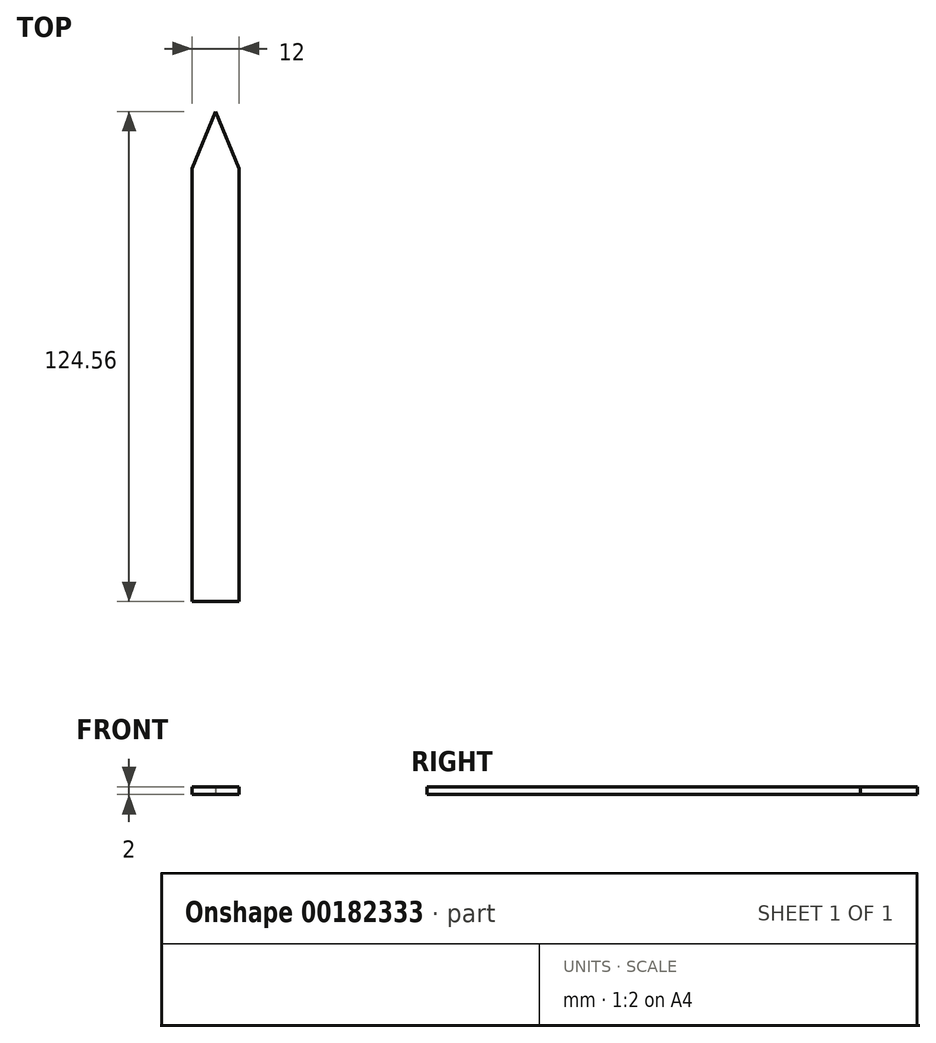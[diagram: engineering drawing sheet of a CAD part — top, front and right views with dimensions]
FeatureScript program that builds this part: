
annotation { "Feature Type Name" : "Feature", "Feature Type Description" : "" }
export const myFeature = defineFeature(function(context is Context, id is Id, definition is map)
    precondition{}
    {
        {
            var Q0;
            Q0=qCreatedBy(makeId("Top.planeOp"),FACE);
            var sketch = newSketch(context, id + "F0", { "sketchPlane" : qUnion([Q0])});
            skLineSegment(sketch, "E0.bottom", {"start": v(-6, -55) * mm, "end": v(0, -55.01) * mm});
            skLineSegment(sketch, "E0.left", {"start": v(-6, -55) * mm, "end": v(-6, 55.02) * mm});
            skLineSegment(sketch, "E0.right", {"start": v(6, -55.02) * mm, "end": v(6, 55) * mm});
            skPoint(sketch, "E0.middle", {"position": v(0, 0) * mm});
            skLineSegment(sketch, "E1.0", {"start": v(0, 69.54) * mm, "end": v(-6, 55.02) * mm});
            skLineSegment(sketch, "E1.2", {"start": v(6, 55) * mm, "end": v(0, 69.54) * mm});
            skPoint(sketch, "E1.0.midPoint", {"position": v(-6, 55.02) * mm});
            skLineSegment(sketch, "E2", {"start": v(0, -55.01) * mm, "end": v(6, -55.02) * mm});
            skSolve(sketch);
        }
        {
            var Q0;
            Q0 = qSketchRegion(id + "F0", true);
            extrude(context, id + "F1", {"entities" : qUnion([Q0]), "depth" : 2 * mm});
        }
    });
